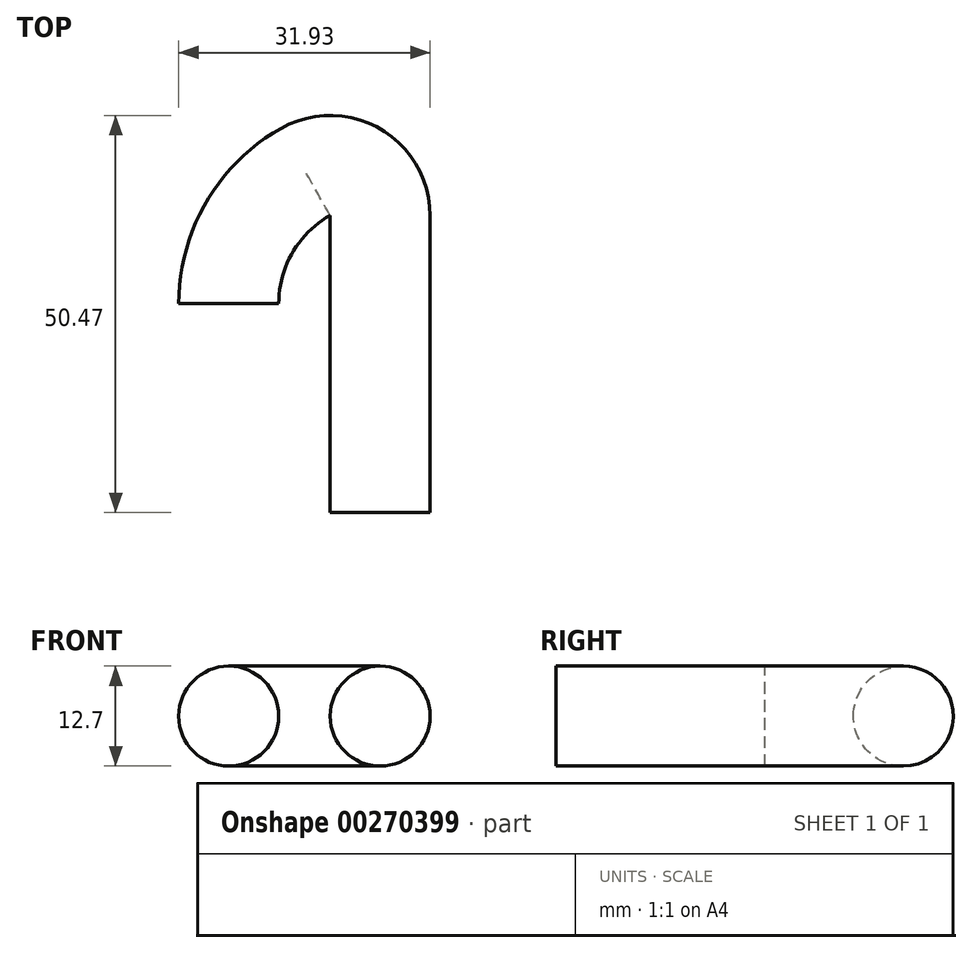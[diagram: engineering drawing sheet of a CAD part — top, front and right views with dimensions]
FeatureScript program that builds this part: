
annotation { "Feature Type Name" : "Feature", "Feature Type Description" : "" }
export const myFeature = defineFeature(function(context is Context, id is Id, definition is map)
    precondition{}
    {
        {
            var Q0;
            Q0=qCreatedBy(makeId("Top.planeOp"),FACE);
            var sketch = newSketch(context, id + "F0", { "sketchPlane" : qUnion([Q0])});
            skLineSegment(sketch, "E0", {"start": v(0, 0) * mm, "end": v(0, 26.56) * mm});
            skArc(sketch, "E1", {"start": v(-19.23, 26.56) * mm, "mid": v(-16.62, 36.24) * mm, "end": v(-9.48, 43.3) * mm});
            skLineSegment(sketch, "E2", {"start": v(0, 37.77) * mm, "end": v(0, 26.56) * mm});
            skPoint(sketch, "E3.visualSharp", {"position": v(0, 45.8) * mm});
            skArc(sketch, "E3.filletArc", {"start": v(0, 37.77) * mm, "mid": v(-3.15, 43.25) * mm, "end": v(-9.48, 43.3) * mm});
            skSolve(sketch);
        }
        {
            var Q0;
            Q0=qCreatedBy(makeId("Front.planeOp"),FACE);
            var sketch = newSketch(context, id + "F1", { "sketchPlane" : qUnion([Q0])});
            skCircle(sketch, "E4", {"center": v(0, 0) * mm, "radius": 6.35 * mm});
            skSolve(sketch);
        }
        {
            var Q0;
            Q0=makeQuery(id+"F1.imprint","IMPRINT",FACE,{"disambiguationData":[TD([[makeQuery(id+"F1.imprint","IMPRINT",EDGE,{"derivedFrom":sQuery(id+"F1.wireOp",EDGE,"E4")}),1.0]])]});
            var Q1;
            Q1=sQuery(id+"F0.wireOp",EDGE,"E1");
            var Q2;
            Q2=sQuery(id+"F0.wireOp",EDGE,"E3.filletArc");
            var Q3;
            Q3=sQuery(id+"F0.wireOp",EDGE,"E2");
            var Q4;
            Q4=sQuery(id+"F0.wireOp",EDGE,"E0");
            sweep(context, id + "F2", {"profiles" : qUnion([Q0]), "path" : qUnion([Q1, Q2, Q3, Q4])});
        }
    });
